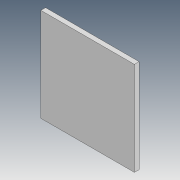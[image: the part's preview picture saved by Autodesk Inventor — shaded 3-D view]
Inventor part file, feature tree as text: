
AUTODESK INVENTOR PART (.ipt)
format: ipt  version: 2021 (Build 250183000, 183)  size: 75,776 bytes
history: native  units: in
note: dims shown in document units (in); Inventor stores cm internally (conversion verified against a paired STEP export)
features: other x1, extrude x1, sketch x1
ambient origin geometry x8: Origin, YZ Plane, XZ Plane, XY Plane, X Axis, Y Axis, Z Axis, Center Point
bodies: Body1 (feature_tree)
feature tree (3):
  other  "Sólido1"
  extrude  "Extrusão1"  Depth=7.874in
  sketch  "Esboço1"  dims[d0=7.874in d1=7.874in d2=0.3937in d3=0.0in]
